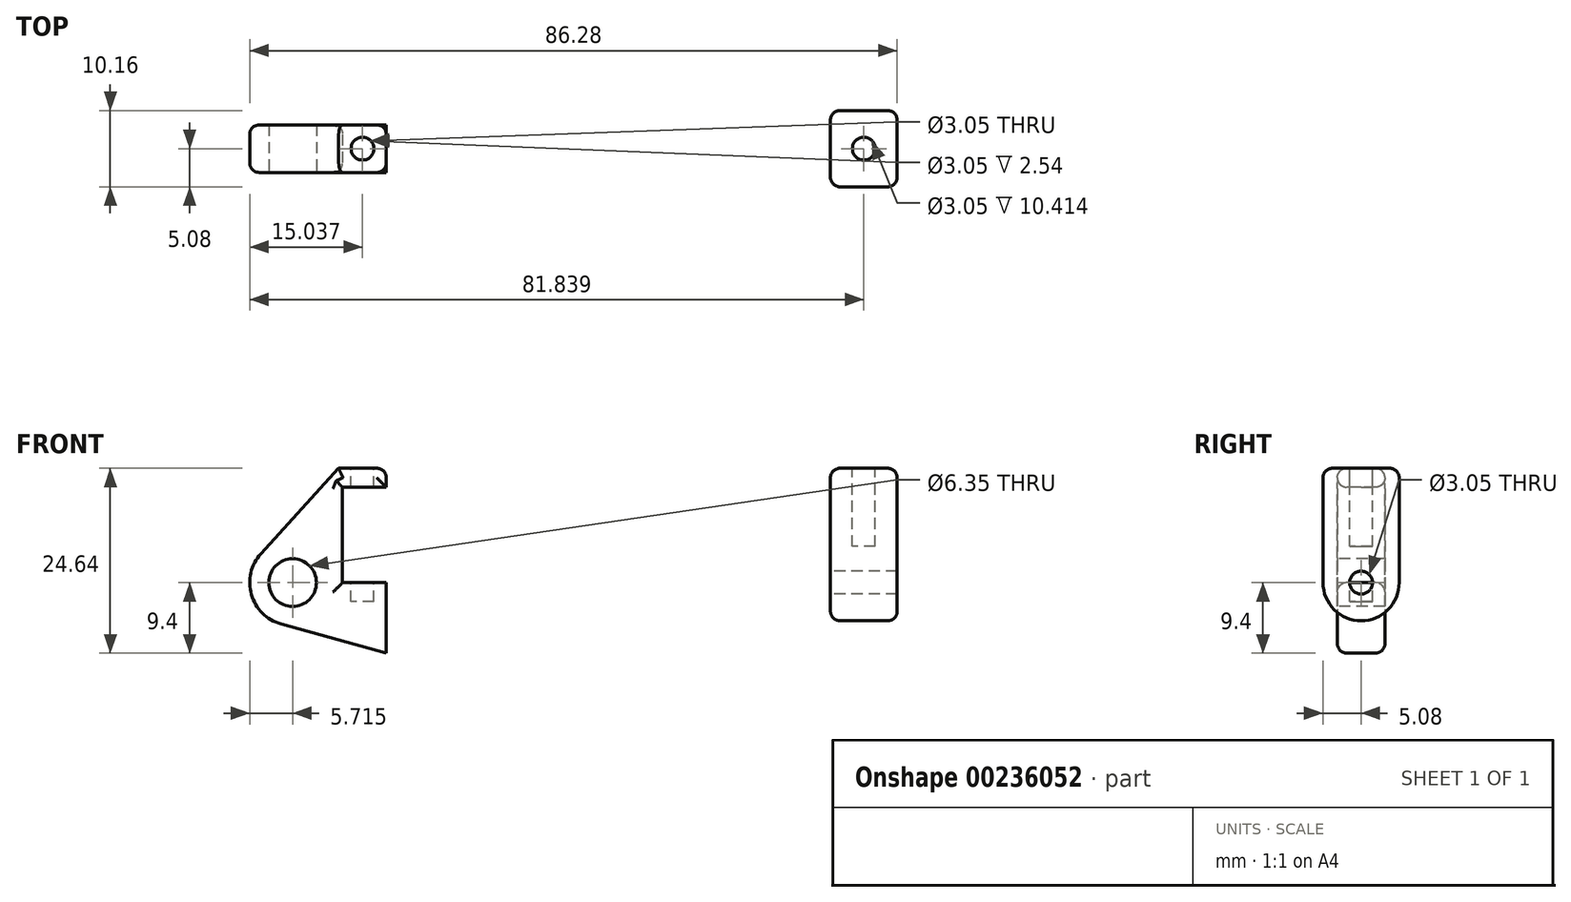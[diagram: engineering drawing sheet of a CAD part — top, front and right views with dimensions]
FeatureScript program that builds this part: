
annotation { "Feature Type Name" : "Feature", "Feature Type Description" : "" }
export const myFeature = defineFeature(function(context is Context, id is Id, definition is map)
    precondition{}
    {
        {
            var Q0;
            Q0=qCreatedBy(makeId("Front.planeOp"),FACE);
            var sketch = newSketch(context, id + "F0", { "sketchPlane" : qUnion([Q0])});
            skLineSegment(sketch, "E0", {"start": v(0, 0) * mm, "end": v(0, 12.7) * mm});
            skLineSegment(sketch, "E1", {"start": v(0, 12.7) * mm, "end": v(10.16, 12.7) * mm});
            skLineSegment(sketch, "E2", {"start": v(10.16, 12.7) * mm, "end": v(10.16, 10.16) * mm});
            skLineSegment(sketch, "E3", {"start": v(10.16, 10.16) * mm, "end": v(56.13, 10.16) * mm});
            skLineSegment(sketch, "E4", {"start": v(56.13, 10.16) * mm, "end": v(56.13, 12.7) * mm});
            skLineSegment(sketch, "E5", {"start": v(56.13, 12.7) * mm, "end": v(66.3, 12.7) * mm});
            skLineSegment(sketch, "E6", {"start": v(66.3, 12.7) * mm, "end": v(66.3, 0) * mm});
            skLineSegment(sketch, "E7", {"start": v(66.3, 0) * mm, "end": v(0, 0) * mm});
            skLineSegment(sketch, "E8", {"start": v(5.84, 15.24) * mm, "end": v(-0.5, 15.24) * mm});
            skLineSegment(sketch, "E9", {"start": v(-0.5, 15.24) * mm, "end": v(-10.88, 3.85) * mm});
            skLineSegment(sketch, "E10", {"start": v(0, 0) * mm, "end": v(-6.65, 0) * mm});
            skCircle(sketch, "E11", {"center": v(-6.65, 0) * mm, "radius": 5.72 * mm});
            skCircle(sketch, "E12", {"center": v(-6.65, 0) * mm, "radius": 3.18 * mm});
            skLineSegment(sketch, "E13", {"start": v(5.84, 15.24) * mm, "end": v(5.84, -9.4) * mm});
            skLineSegment(sketch, "E14", {"start": v(5.84, -9.4) * mm, "end": v(-8.18, -5.5) * mm});
            skSolve(sketch);
        }
        {
            var Q0;
            Q0=sQuery(id+"F0.wireOp",EDGE,"E3");
            var Q1;
            Q1=sQuery(id+"F0.wireOp",EDGE,"E1");
            var Q2;
            Q2=sQuery(id+"F0.wireOp",EDGE,"E2");
            var Q3;
            Q3=sQuery(id+"F0.wireOp",EDGE,"E4");
            var Q4;
            Q4=sQuery(id+"F0.wireOp",EDGE,"E5");
            var Q5;
            Q5=sQuery(id+"F0.wireOp",EDGE,"E6");
            var Q6;
            Q6=sQuery(id+"F0.wireOp",EDGE,"E0");
            var Q7;
            Q7=sQuery(id+"F0.wireOp",EDGE,"E7");
            revolve(context, id + "F1", {"bodyType" : ToolBodyType.SURFACE, "surfaceEntities" : qUnion([Q0, Q1, Q2, Q3, Q4, Q5, Q6]), "axis" : qUnion([Q7]), "revolveType" : RevolveType.FULL});
        }
        {
            var Q0;
            {var subQ3=sQuery(id+"F0.wireOp",EDGE,"E0");Q0=makeQuery(id+"F0.imprint","IMPRINT",FACE,{"disambiguationData":[TD([[makeQuery(id+"F0.imprint","IMPRINT",EDGE,{"derivedFrom":subQ3}),1.0]])]});}
            var Q1;
            {var subQ4=sQuery(id+"F0.wireOp",EDGE,"E12");Q1=makeQuery(id+"F0.imprint","IMPRINT",FACE,{"disambiguationData":[TD([[makeQuery(id+"F0.imprint","IMPRINT",EDGE,{"derivedFrom":subQ4}),-1.0]])]});}
            var Q2;
            {var subQ0=sQuery(id+"F0.wireOp",EDGE,"E14");Q2=makeQuery(id+"F0.imprint","IMPRINT",FACE,{"disambiguationData":[TD([[makeQuery(id+"F0.imprint","IMPRINT",EDGE,{"derivedFrom":subQ0}),-1.0]])]});}
            extrude(context, id + "F2", {"entities" : qUnion([Q0, Q1, Q2]), "endBound" : BoundingType.SYMMETRIC, "oppositeDirection" : true, "depth" : 6.35 * mm});
        }
        {
            var Q0;
            Q0=makeQuery(id+"F1.opRevolve","SWEPT_FACE",FACE,{"disambiguationData":[OSD([sQuery(id+"F0.wireOp",EDGE,"E6")])]});
            var sketch = newSketch(context, id + "F3", { "sketchPlane" : qUnion([Q0])});
            skCircle(sketch, "E15", {"center": v(0, 0) * mm, "radius": 1.52 * mm});
            skCircle(sketch, "E16", {"center": v(0, 0) * mm, "radius": 5.08 * mm});
            skLineSegment(sketch, "E17", {"start": v(-5.08, 0) * mm, "end": v(-5.08, 15.24) * mm});
            skLineSegment(sketch, "E18", {"start": v(5.08, 15.24) * mm, "end": v(5.08, 0) * mm});
            skLineSegment(sketch, "E19", {"start": v(-5.08, 15.24) * mm, "end": v(5.08, 15.24) * mm});
            skSolve(sketch);
        }
        {
            var Q0;
            Q0 = qSketchRegion(id + "F3", true);
            extrude(context, id + "F4", {"entities" : qUnion([Q0]), "depth" : 7.62 * mm, "hasSecondDirection" : true, "secondDirectionOppositeDirection" : true, "secondDirectionDepth" : 1.27 * mm});
        }
        {
            var Q0;
            Q0=makeQuery(id+"F3.imprint","IMPRINT",FACE,{"disambiguationData":[TD([[makeQuery(id+"F3.imprint","IMPRINT",EDGE,{"derivedFrom":sQuery(id+"F3.wireOp",EDGE,"E15")}),1.0]])]});
            var Q1;
            Q1=sQuery(id+"F3.wireOp",EDGE,"E15");
            extrude(context, id + "F5", {"entities" : qUnion([Q0]), "operationType" : NewBodyOperationType.REMOVE, "surfaceEntities" : qUnion([Q1]), "oppositeDirection" : true, "depth" : 56.13 * mm});
        }
        {
            var Q0;
            Q0=makeQuery(id+"F4.opExtrude","SWEPT_FACE",FACE,{"disambiguationData":[OSD([sQuery(id+"F3.wireOp",EDGE,"E19")])]});
            var sketch = newSketch(context, id + "F6", { "sketchPlane" : qUnion([Q0])});
            skCircle(sketch, "E20", {"center": v(69.47, 0) * mm, "radius": 1.52 * mm});
            skSolve(sketch);
        }
        {
            var Q0;
            Q0=makeQuery(id+"F2.opExtrude","SWEPT_FACE",FACE,{"disambiguationData":[OSD([sQuery(id+"F0.wireOp",EDGE,"E8")])]});
            var sketch = newSketch(context, id + "F7", { "sketchPlane" : qUnion([Q0])});
            skCircle(sketch, "E21", {"center": v(2.67, 0) * mm, "radius": 1.52 * mm});
            skSolve(sketch);
        }
        {
            var Q0;
            Q0 = qSketchRegion(id + "F7", true);
            extrude(context, id + "F8", {"entities" : qUnion([Q0]), "operationType" : NewBodyOperationType.REMOVE, "oppositeDirection" : true, "depth" : 17.78 * mm});
        }
        {
            var Q0;
            Q0 = qSketchRegion(id + "F6", true);
            extrude(context, id + "F9", {"entities" : qUnion([Q0]), "operationType" : NewBodyOperationType.REMOVE, "oppositeDirection" : true, "depth" : 10.4 * mm});
        }
        {
            var Q0;
            Q0=makeQuery(id+"F2.opExtrude","CAP_EDGE",EDGE,{"disambiguationData":[OSD([sQuery(id+"F0.wireOp",EDGE,"E9")])],"isStart":true});
            var Q1;
            Q1=makeQuery(id+"F2.opExtrude","CAP_EDGE",EDGE,{"disambiguationData":[OSD([sQuery(id+"F0.wireOp",EDGE,"E8")])],"isStart":true});
            var Q2;
            {var subQ0=sQuery(id+"F0.wireOp",EDGE,"E13");Q2=makeQuery(id+"F2.opExtrude","CAP_EDGE",EDGE,{"disambiguationData":[OSD([subQ0]),TDD([makeQuery(id+"F0.imprint","IMPRINT",EDGE,{"disambiguationData":[TD([[makeQuery(id+"F0.imprint","INTERSECT",VERTEX,{"derivedFrom":[sQuery(id+"F0.wireOp",EDGE,"E8"),subQ0]}),-1.0]])],"derivedFrom":subQ0})])],"isStart":true});}
            var Q3;
            Q3=makeQuery(id+"F2.opExtrude","CAP_EDGE",EDGE,{"disambiguationData":[OSD([sQuery(id+"F0.wireOp",EDGE,"E1")])],"isStart":true});
            var Q4;
            Q4=makeQuery(id+"F2.opExtrude","CAP_EDGE",EDGE,{"disambiguationData":[OSD([sQuery(id+"F0.wireOp",EDGE,"E0")])],"isStart":true});
            var Q5;
            Q5=makeQuery(id+"F2.opExtrude","CAP_EDGE",EDGE,{"disambiguationData":[OSD([sQuery(id+"F0.wireOp",EDGE,"E14")])],"isStart":true});
            var Q6;
            Q6=makeQuery(id+"F2.opExtrude","CAP_EDGE",EDGE,{"disambiguationData":[OSD([sQuery(id+"F0.wireOp",EDGE,"E11")])],"isStart":true});
            var Q7;
            Q7=makeQuery(id+"F2.opExtrude","CAP_EDGE",EDGE,{"disambiguationData":[OSD([sQuery(id+"F0.wireOp",EDGE,"E9")])],"isStart":false});
            var Q8;
            Q8=makeQuery(id+"F2.opExtrude","CAP_EDGE",EDGE,{"disambiguationData":[OSD([sQuery(id+"F0.wireOp",EDGE,"E11")])],"isStart":false});
            var Q9;
            Q9=makeQuery(id+"F2.opExtrude","CAP_EDGE",EDGE,{"disambiguationData":[OSD([sQuery(id+"F0.wireOp",EDGE,"E14")])],"isStart":false});
            var Q10;
            Q10=makeQuery(id+"F2.opExtrude","CAP_EDGE",EDGE,{"disambiguationData":[OSD([sQuery(id+"F0.wireOp",EDGE,"E8")])],"isStart":false});
            var Q11;
            {var subQ0=sQuery(id+"F0.wireOp",EDGE,"E13");Q11=makeQuery(id+"F2.opExtrude","CAP_EDGE",EDGE,{"disambiguationData":[OSD([subQ0]),TDD([makeQuery(id+"F0.imprint","IMPRINT",EDGE,{"disambiguationData":[TD([[makeQuery(id+"F0.imprint","INTERSECT",VERTEX,{"derivedFrom":[sQuery(id+"F0.wireOp",EDGE,"E8"),subQ0]}),-1.0]])],"derivedFrom":subQ0})])],"isStart":false});}
            var Q12;
            Q12=makeQuery(id+"F2.opExtrude","CAP_EDGE",EDGE,{"disambiguationData":[OSD([sQuery(id+"F0.wireOp",EDGE,"E1")])],"isStart":false});
            var Q13;
            Q13=makeQuery(id+"F2.opExtrude","CAP_EDGE",EDGE,{"disambiguationData":[OSD([sQuery(id+"F0.wireOp",EDGE,"E0")])],"isStart":false});
            var Q14;
            Q14=makeQuery(id+"F1.opRevolve","SWEPT_EDGE",EDGE,{"disambiguationData":[OSD([sQuery(id+"F0.wireOp",VERTEX,"E2.start")])]});
            var Q15;
            Q15=makeQuery(id+"F1.opRevolve","SWEPT_EDGE",EDGE,{"disambiguationData":[OSD([sQuery(id+"F0.wireOp",VERTEX,"E0.end")])]});
            var Q16;
            Q16=makeQuery(id+"F1.opRevolve","SWEPT_EDGE",EDGE,{"disambiguationData":[OSD([sQuery(id+"F0.wireOp",VERTEX,"E2.end")])]});
            var Q17;
            Q17=makeQuery(id+"F1.opRevolve","SWEPT_EDGE",EDGE,{"disambiguationData":[OSD([sQuery(id+"F0.wireOp",VERTEX,"E5.start")])]});
            var Q18;
            Q18=makeQuery(id+"F1.opRevolve","SWEPT_EDGE",EDGE,{"disambiguationData":[OSD([sQuery(id+"F0.wireOp",VERTEX,"E4.start")])]});
            var Q19;
            Q19=makeQuery(id+"F1.opRevolve","SWEPT_EDGE",EDGE,{"disambiguationData":[OSD([sQuery(id+"F0.wireOp",VERTEX,"E6.start")])]});
            var Q20;
            Q20=makeQuery(id+"F4.opExtrude","SWEPT_EDGE",EDGE,{"disambiguationData":[OSD([sQuery(id+"F3.wireOp",EDGE,"E18"),sQuery(id+"F3.wireOp",EDGE,"E19")])]});
            var Q21;
            Q21=makeQuery(id+"F4.opExtrude","CAP_EDGE",EDGE,{"disambiguationData":[OSD([sQuery(id+"F3.wireOp",EDGE,"E19")])],"isStart":false});
            var Q22;
            Q22=makeQuery(id+"F4.opExtrude","SWEPT_EDGE",EDGE,{"disambiguationData":[OSD([sQuery(id+"F3.wireOp",EDGE,"E17"),sQuery(id+"F3.wireOp",EDGE,"E19")])]});
            var Q23;
            Q23=makeQuery(id+"F4.opExtrude","CAP_EDGE",EDGE,{"disambiguationData":[OSD([sQuery(id+"F3.wireOp",EDGE,"E19")])],"isStart":true});
            var Q24;
            Q24=makeQuery(id+"F4.opExtrude","CAP_EDGE",EDGE,{"disambiguationData":[OSD([sQuery(id+"F3.wireOp",EDGE,"E18")])],"isStart":false});
            var Q25;
            Q25=makeQuery(id+"F4.opExtrude","CAP_EDGE",EDGE,{"disambiguationData":[OSD([sQuery(id+"F3.wireOp",EDGE,"E16")])],"isStart":false});
            var Q26;
            Q26=makeQuery(id+"F4.opExtrude","CAP_EDGE",EDGE,{"disambiguationData":[OSD([sQuery(id+"F3.wireOp",EDGE,"E17")])],"isStart":false});
            fillet(context, id + "F10", {"entities" : qUnion([Q0, Q1, Q2, Q3, Q4, Q5, Q6, Q7, Q8, Q9, Q10, Q11, Q12, Q13, Q14, Q15, Q16, Q17, Q18, Q19, Q20, Q21, Q22, Q23, Q24, Q25, Q26]), "radius" : 1.27 * mm, "tangentPropagation" : true, "allowEdgeOverflow" : false});
        }
        {
            var Q0;
            Q0=makeQuery(id+"F2.opExtrude","SWEPT_EDGE",EDGE,{"disambiguationData":[OSD([sQuery(id+"F0.wireOp",EDGE,"E8"),sQuery(id+"F0.wireOp",EDGE,"E13")])]});
            fillet(context, id + "F11", {"entities" : qUnion([Q0]), "radius" : 1.27 * mm, "tangentPropagation" : true, "allowEdgeOverflow" : false});
        }
        {
            var Q0;
            Q0=makeQuery(id+"F2.opExtrude","CAP_EDGE",EDGE,{"disambiguationData":[OSD([sQuery(id+"F0.wireOp",EDGE,"E7")])],"isStart":true});
            fillet(context, id + "F12", {"entities" : qUnion([Q0]), "radius" : 1.27 * mm, "tangentPropagation" : true, "allowEdgeOverflow" : false});
        }
        {
            var Q0;
            Q0=makeQuery(id+"F2.opExtrude","CAP_EDGE",EDGE,{"disambiguationData":[OSD([sQuery(id+"F0.wireOp",EDGE,"E7")])],"isStart":false});
            fillet(context, id + "F13", {"entities" : qUnion([Q0]), "radius" : 1.27 * mm, "tangentPropagation" : true, "allowEdgeOverflow" : false});
        }
        {
            var Q0;
            {var subQ0=sQuery(id+"F3.wireOp",EDGE,"E19");Q0=makeQuery(id+"F10.opFillet","BLEND_EDGE",EDGE,{"blendedFrom":[makeQuery(id+"F4.opExtrude","SWEPT_EDGE",EDGE,{"disambiguationData":[OSD([sQuery(id+"F3.wireOp",EDGE,"E18"),subQ0])]}),makeQuery(id+"F4.opExtrude","CAP_EDGE",EDGE,{"disambiguationData":[OSD([subQ0])],"isStart":true})],"blendedInto":[]});}
            var Q1;
            {var subQ0=sQuery(id+"F3.wireOp",EDGE,"E19");Q1=makeQuery(id+"F10.opFillet","BLEND_EDGE",EDGE,{"blendedFrom":[makeQuery(id+"F4.opExtrude","SWEPT_EDGE",EDGE,{"disambiguationData":[OSD([sQuery(id+"F3.wireOp",EDGE,"E17"),subQ0])]}),makeQuery(id+"F4.opExtrude","CAP_EDGE",EDGE,{"disambiguationData":[OSD([subQ0])],"isStart":true})],"blendedInto":[]});}
            fillet(context, id + "F14", {"entities" : qUnion([Q0, Q1]), "radius" : 1.27 * mm, "tangentPropagation" : true, "allowEdgeOverflow" : false});
        }
    });
